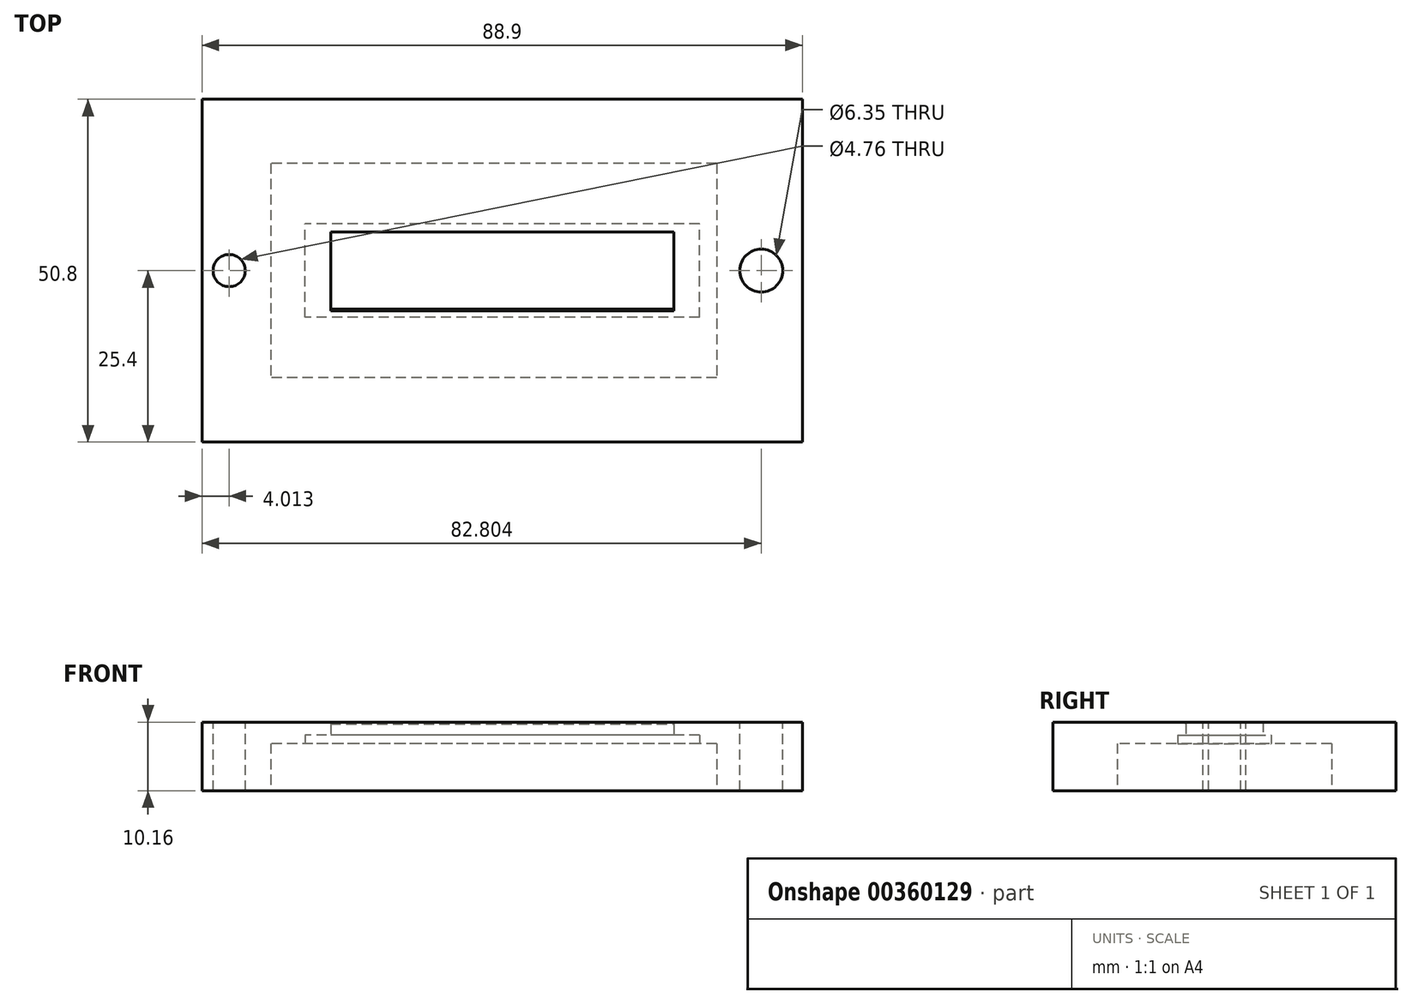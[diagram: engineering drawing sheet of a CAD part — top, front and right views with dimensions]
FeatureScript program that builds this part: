
annotation { "Feature Type Name" : "Feature", "Feature Type Description" : "" }
export const myFeature = defineFeature(function(context is Context, id is Id, definition is map)
    precondition{}
    {
        {
            var Q0;
            Q0=qCreatedBy(makeId("Top.planeOp"),FACE);
            var sketch = newSketch(context, id + "F0", { "sketchPlane" : qUnion([Q0])});
            skLineSegment(sketch, "E0.bottom", {"start": v(0, 0) * mm, "end": v(88.9, 0) * mm});
            skLineSegment(sketch, "E0.top", {"start": v(0, 50.8) * mm, "end": v(88.9, 50.8) * mm});
            skLineSegment(sketch, "E0.left", {"start": v(0, 0) * mm, "end": v(0, 50.8) * mm});
            skLineSegment(sketch, "E0.right", {"start": v(88.9, 0) * mm, "end": v(88.9, 50.8) * mm});
            skSolve(sketch);
        }
        {
            var Q0;
            Q0 = qSketchRegion(id + "F0", true);
            extrude(context, id + "F1", {"entities" : qUnion([Q0]), "depth" : 10.16 * mm});
        }
        {
            var Q0;
            Q0=makeQuery(id+"F1.opExtrude","CAP_FACE",FACE,{"disambiguationData":[OSD([sQuery(id+"F0.wireOp",EDGE,"E0.bottom"),sQuery(id+"F0.wireOp",EDGE,"E0.top"),sQuery(id+"F0.wireOp",EDGE,"E0.left"),sQuery(id+"F0.wireOp",EDGE,"E0.right")])],"isStart":false});
            var sketch = newSketch(context, id + "F2", { "sketchPlane" : qUnion([Q0])});
            skCircle(sketch, "E1", {"center": v(4.01, 25.4) * mm, "radius": 2.38 * mm});
            skPoint(sketch, "E1.centerSnap0", {"position": v(0, 25.4) * mm});
            skCircle(sketch, "E2", {"center": v(82.8, 25.4) * mm, "radius": 3.18 * mm});
            skSolve(sketch);
        }
        {
            var Q0;
            Q0 = qSketchRegion(id + "F2", true);
            extrude(context, id + "F3", {"entities" : qUnion([Q0]), "operationType" : NewBodyOperationType.REMOVE, "oppositeDirection" : true, "depth" : 25.4 * mm});
        }
        {
            var Q0;
            Q0=makeQuery(id+"F1.opExtrude","CAP_FACE",FACE,{"disambiguationData":[OSD([sQuery(id+"F0.wireOp",EDGE,"E0.bottom"),sQuery(id+"F0.wireOp",EDGE,"E0.top"),sQuery(id+"F0.wireOp",EDGE,"E0.left"),sQuery(id+"F0.wireOp",EDGE,"E0.right")])],"isStart":true});
            var sketch = newSketch(context, id + "F4", { "sketchPlane" : qUnion([Q0])});
            skLineSegment(sketch, "E3.bottom", {"start": v(76.2, -41.28) * mm, "end": v(10.16, -41.28) * mm});
            skLineSegment(sketch, "E3.top", {"start": v(76.2, -9.53) * mm, "end": v(10.16, -9.53) * mm});
            skLineSegment(sketch, "E3.left", {"start": v(76.2, -41.28) * mm, "end": v(76.2, -9.53) * mm});
            skLineSegment(sketch, "E3.right", {"start": v(10.16, -41.28) * mm, "end": v(10.16, -9.53) * mm});
            skSolve(sketch);
        }
        {
            var Q0;
            Q0 = qSketchRegion(id + "F4", true);
            extrude(context, id + "F5", {"entities" : qUnion([Q0]), "operationType" : NewBodyOperationType.REMOVE, "oppositeDirection" : true, "depth" : 7 * mm});
        }
        {
            var Q0;
            Q0=makeQuery(id+"F5.boolean.opBoolean","COPY",FACE,{"derivedFrom":makeQuery(id+"F5.opExtrude","CAP_FACE",FACE,{"disambiguationData":[OSD([sQuery(id+"F4.wireOp",EDGE,"E3.bottom"),sQuery(id+"F4.wireOp",EDGE,"E3.top"),sQuery(id+"F4.wireOp",EDGE,"E3.left"),sQuery(id+"F4.wireOp",EDGE,"E3.right")])],"isStart":false})});
            var sketch = newSketch(context, id + "F6", { "sketchPlane" : qUnion([Q0])});
            skLineSegment(sketch, "E4.bottom", {"start": v(73.66, -18.47) * mm, "end": v(15.24, -18.47) * mm});
            skLineSegment(sketch, "E4.top", {"start": v(73.66, -32.33) * mm, "end": v(15.24, -32.33) * mm});
            skLineSegment(sketch, "E4.left", {"start": v(73.66, -18.47) * mm, "end": v(73.66, -32.33) * mm});
            skLineSegment(sketch, "E4.right", {"start": v(15.24, -18.47) * mm, "end": v(15.24, -32.33) * mm});
            skPoint(sketch, "E4.middle", {"position": v(44.45, -25.4) * mm});
            skSolve(sketch);
        }
        {
            var Q0;
            Q0 = qSketchRegion(id + "F6", true);
            extrude(context, id + "F7", {"entities" : qUnion([Q0]), "operationType" : NewBodyOperationType.REMOVE, "oppositeDirection" : true, "depth" : 1.27 * mm});
        }
        {
            var Q0;
            Q0=makeQuery(id+"F7.boolean.opBoolean","COPY",FACE,{"derivedFrom":makeQuery(id+"F7.opExtrude","CAP_FACE",FACE,{"disambiguationData":[OSD([sQuery(id+"F6.wireOp",EDGE,"E4.bottom"),sQuery(id+"F6.wireOp",EDGE,"E4.top"),sQuery(id+"F6.wireOp",EDGE,"E4.left"),sQuery(id+"F6.wireOp",EDGE,"E4.right")])],"isStart":false})});
            var sketch = newSketch(context, id + "F8", { "sketchPlane" : qUnion([Q0])});
            skLineSegment(sketch, "E5.bottom", {"start": v(69.85, -19.69) * mm, "end": v(19.05, -19.69) * mm});
            skLineSegment(sketch, "E5.top", {"start": v(69.85, -31.11) * mm, "end": v(19.05, -31.12) * mm});
            skLineSegment(sketch, "E5.left", {"start": v(69.85, -19.69) * mm, "end": v(69.85, -31.11) * mm});
            skLineSegment(sketch, "E5.right", {"start": v(19.05, -19.69) * mm, "end": v(19.05, -31.12) * mm});
            skSolve(sketch);
        }
        {
            var Q0;
            Q0 = qSketchRegion(id + "F8", true);
            extrude(context, id + "F9", {"entities" : qUnion([Q0]), "operationType" : NewBodyOperationType.REMOVE, "oppositeDirection" : true, "depth" : 25.4 * mm});
        }
        {
            var Q0;
            Q0=makeQuery(id+"F9.boolean.opBoolean","COPY",EDGE,{"derivedFrom":makeQuery(id+"F9.opExtrude","CAP_EDGE",EDGE,{"disambiguationData":[OSD([sQuery(id+"F8.wireOp",EDGE,"E5.top")])],"isStart":true})});
            var Q1;
            Q1=makeQuery(id+"F9.boolean.opBoolean","COPY",EDGE,{"derivedFrom":makeQuery(id+"F9.opExtrude","CAP_EDGE",EDGE,{"disambiguationData":[OSD([sQuery(id+"F8.wireOp",EDGE,"E5.left")])],"isStart":true})});
            var Q2;
            Q2=makeQuery(id+"F9.boolean.opBoolean","INTERSECT",EDGE,{"derivedFrom":[makeQuery(id+"F1.opExtrude","CAP_FACE",FACE,{"disambiguationData":[OSD([sQuery(id+"F0.wireOp",EDGE,"E0.bottom"),sQuery(id+"F0.wireOp",EDGE,"E0.top"),sQuery(id+"F0.wireOp",EDGE,"E0.left"),sQuery(id+"F0.wireOp",EDGE,"E0.right")])],"isStart":false}),makeQuery(id+"F9.opExtrude","SWEPT_FACE",FACE,{"disambiguationData":[OSD([sQuery(id+"F8.wireOp",EDGE,"E5.bottom")])]})]});
            var Q3;
            Q3=makeQuery(id+"F9.boolean.opBoolean","COPY",EDGE,{"derivedFrom":makeQuery(id+"F9.opExtrude","CAP_EDGE",EDGE,{"disambiguationData":[OSD([sQuery(id+"F8.wireOp",EDGE,"E5.right")])],"isStart":true})});
            chamfer(context, id + "F10", {"entities" : qUnion([Q0, Q1, Q2, Q3]), "width" : 0.25 * mm, "tangentPropagation" : true});
        }
    });
